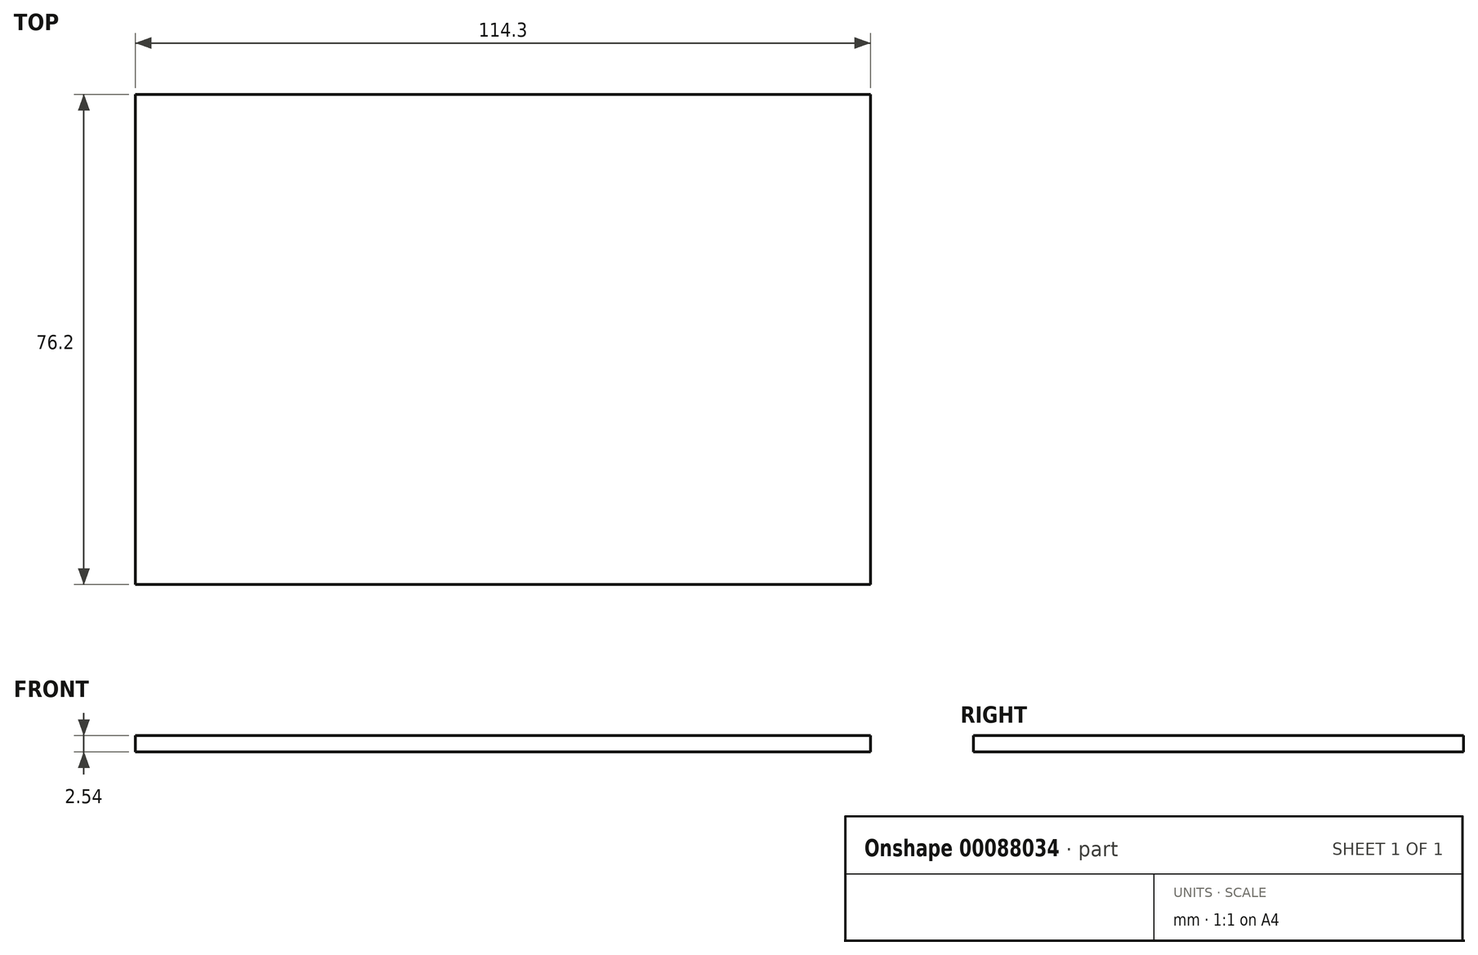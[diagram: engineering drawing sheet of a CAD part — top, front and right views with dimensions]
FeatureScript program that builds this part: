
annotation { "Feature Type Name" : "Feature", "Feature Type Description" : "" }
export const myFeature = defineFeature(function(context is Context, id is Id, definition is map)
    precondition{}
    {
        {
            var Q0;
            Q0=qCreatedBy(makeId("Top.planeOp"),FACE);
            var sketch = newSketch(context, id + "F0", { "sketchPlane" : qUnion([Q0])});
            skLineSegment(sketch, "E0.bottom", {"start": v(57.15, -38.1) * mm, "end": v(-57.15, -38.1) * mm});
            skLineSegment(sketch, "E0.top", {"start": v(57.15, 38.1) * mm, "end": v(-57.15, 38.1) * mm});
            skLineSegment(sketch, "E0.left", {"start": v(57.15, -38.1) * mm, "end": v(57.15, 38.1) * mm});
            skLineSegment(sketch, "E0.right", {"start": v(-57.15, -38.1) * mm, "end": v(-57.15, 38.1) * mm});
            skPoint(sketch, "E0.middle", {"position": v(0, 0) * mm});
            skSolve(sketch);
        }
        {
            var Q0;
            Q0=makeQuery(id+"F0.imprint","IMPRINT",FACE,{"disambiguationData":[TD([[makeQuery(id+"F0.imprint","IMPRINT",EDGE,{"derivedFrom":sQuery(id+"F0.wireOp",EDGE,"E0.bottom")}),-1.0]])]});
            extrude(context, id + "F1", {"entities" : qUnion([Q0]), "depth" : 2.54 * mm});
        }
    });
